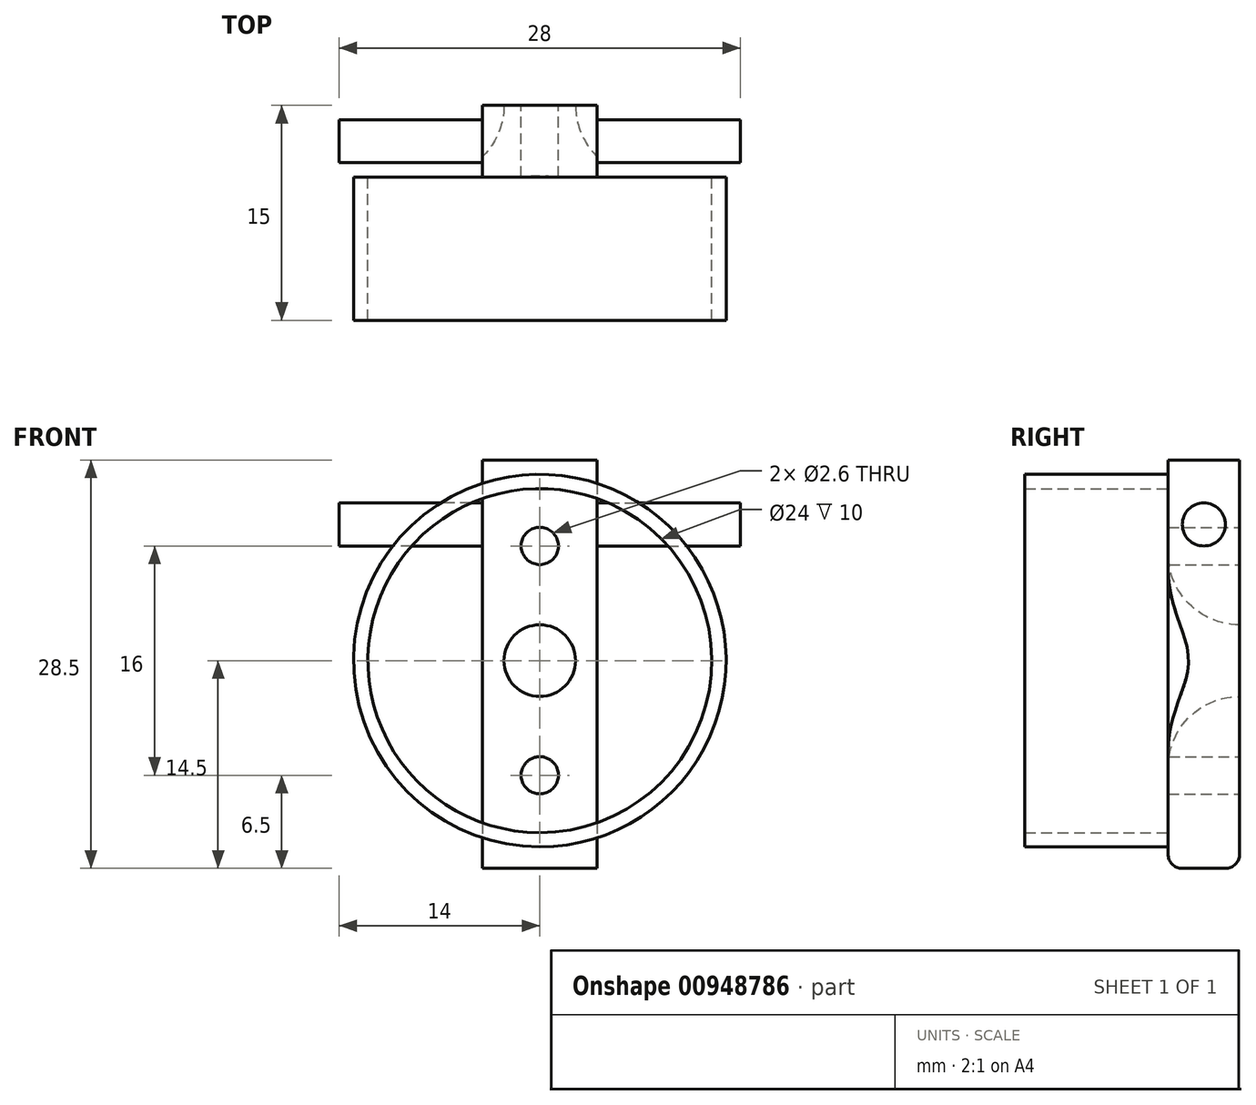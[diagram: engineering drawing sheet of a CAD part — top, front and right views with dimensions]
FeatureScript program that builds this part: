
annotation { "Feature Type Name" : "Feature", "Feature Type Description" : "" }
export const myFeature = defineFeature(function(context is Context, id is Id, definition is map)
    precondition{}
    {
        {
            var Q0;
            Q0=qCreatedBy(makeId("Front.planeOp"),FACE);
            var sketch = newSketch(context, id + "F0", { "sketchPlane" : qUnion([Q0])});
            skLineSegment(sketch, "E0.bottom", {"start": v(14, 14.5) * mm, "end": v(-14, 14.5) * mm});
            skLineSegment(sketch, "E0.top", {"start": v(14, -14.5) * mm, "end": v(-14, -14.5) * mm});
            skLineSegment(sketch, "E0.left", {"start": v(14, 14.5) * mm, "end": v(14, -14.5) * mm});
            skLineSegment(sketch, "E0.right", {"start": v(-14, 14.5) * mm, "end": v(-14, -14.5) * mm});
            skPoint(sketch, "E0.middle", {"position": v(0, 0) * mm});
            skCircle(sketch, "E1", {"center": v(0, 0) * mm, "radius": 12 * mm});
            skCircle(sketch, "E2", {"center": v(0, 0) * mm, "radius": 13 * mm});
            skLineSegment(sketch, "E3", {"start": v(0, 0) * mm, "end": v(0, 8) * mm});
            skLineSegment(sketch, "E4", {"start": v(0, 0) * mm, "end": v(0, -8) * mm});
            skCircle(sketch, "E5", {"center": v(0, 8) * mm, "radius": 1.3 * mm});
            skCircle(sketch, "E6", {"center": v(0, -8) * mm, "radius": 1.3 * mm});
            skCircle(sketch, "E7", {"center": v(0, 0) * mm, "radius": 2.5 * mm});
            skSolve(sketch);
        }
        {
            var Q0;
            Q0=makeQuery(id+"F0.imprint","IMPRINT",FACE,{"disambiguationData":[TD([[makeQuery(id+"F0.imprint","IMPRINT",EDGE,{"derivedFrom":sQuery(id+"F0.wireOp",EDGE,"E1")}),1.0]])]});
            var Q1;
            Q1=makeQuery(id+"F0.imprint","IMPRINT",FACE,{"disambiguationData":[TD([[makeQuery(id+"F0.imprint","IMPRINT",EDGE,{"derivedFrom":sQuery(id+"F0.wireOp",EDGE,"E0.bottom")}),1.0]])]});
            extrude(context, id + "F1", {"entities" : qUnion([Q0, Q1]), "depth" : 5 * mm, "offsetDistance" : 25 * mm});
        }
        {
            var Q0;
            {var subQ0=sQuery(id+"F0.wireOp",EDGE,"jVAeQmTI-I4b5-sMDT-F5OX-ICpV5nC2f3Dc");var subQ1=sQuery(id+"F0.wireOp",EDGE,"E1");var subQ2=makeQuery(id+"F0.imprint","INTERSECT",VERTEX,{"disambiguationData":[OD(1.0)],"derivedFrom":[subQ1,subQ0]});Q0=makeQuery(id+"F0.imprint","IMPRINT",FACE,{"disambiguationData":[TD([[makeQuery(id+"F0.imprint","IMPRINT",EDGE,{"disambiguationData":[TD([[subQ2,-1.0]])],"derivedFrom":subQ1}),-1.0]])]});}
            var Q1;
            {var subQ0=sQuery(id+"F0.wireOp",EDGE,"c9JZCTCg-LH8D-izqR-xvkh-gdVYYUprtubE");var subQ1=sQuery(id+"F0.wireOp",EDGE,"E1");var subQ2=makeQuery(id+"F0.imprint","INTERSECT",VERTEX,{"disambiguationData":[OD(0.0)],"derivedFrom":[subQ1,subQ0]});Q1=makeQuery(id+"F0.imprint","IMPRINT",FACE,{"disambiguationData":[TD([[makeQuery(id+"F0.imprint","IMPRINT",EDGE,{"disambiguationData":[TD([[subQ2,-1.0]])],"derivedFrom":subQ1}),-1.0]])]});}
            extrude(context, id + "F2", {"entities" : qUnion([Q0, Q1]), "operationType" : NewBodyOperationType.ADD, "depth" : 15 * mm, "offsetDistance" : 25 * mm});
        }
        {
            var Q0;
            Q0=makeQuery(id+"F1.opExtrude","CAP_EDGE",EDGE,{"disambiguationData":[OSD([sQuery(id+"F0.wireOp",EDGE,"E7")])],"isStart":false});
            fillet(context, id + "F3", {"entities" : qUnion([Q0]), "radius" : 5 * mm, "tangentPropagation" : true, "allowEdgeOverflow" : false});
        }
        {
            var Q0;
            Q0=makeQuery(id+"F1.opExtrude","SWEPT_FACE",FACE,{"disambiguationData":[OSD([sQuery(id+"F0.wireOp",EDGE,"E0.right")])]});
            var sketch = newSketch(context, id + "F4", { "sketchPlane" : qUnion([Q0])});
            skLineSegment(sketch, "E8", {"start": v(2.5, 14.5) * mm, "end": v(2.5, -14.5) * mm});
            skCircle(sketch, "E9", {"center": v(2.5, 9.5) * mm, "radius": 1.5 * mm});
            skCircle(sketch, "E10", {"center": v(2.5, -10.5) * mm, "radius": 1.5 * mm});
            skSolve(sketch);
        }
        {
            var Q0;
            Q0=makeQuery(id+"F1.opExtrude","SWEPT_FACE",FACE,{"disambiguationData":[OSD([sQuery(id+"F0.wireOp",EDGE,"E0.left")])]});
            var sketch = newSketch(context, id + "F5", { "sketchPlane" : qUnion([Q0])});
            skLineSegment(sketch, "E11", {"start": v(-2.5, 14.5) * mm, "end": v(-2.5, -14.5) * mm});
            skCircle(sketch, "E12", {"center": v(-2.5, 9.5) * mm, "radius": 1.5 * mm});
            skCircle(sketch, "E13", {"center": v(-2.5, -10.5) * mm, "radius": 1.5 * mm});
            skSolve(sketch);
        }
        {
            var Q0;
            {var subQ0=sQuery(id+"F4.wireOp",EDGE,"E9");var subQ1=sQuery(id+"F4.wireOp",EDGE,"E8");var subQ2=makeQuery(id+"F4.imprint","INTERSECT",VERTEX,{"disambiguationData":[OD(0.0)],"derivedFrom":[subQ1,subQ0]});Q0=makeQuery(id+"F4.imprint","IMPRINT",FACE,{"disambiguationData":[TD([[makeQuery(id+"F4.imprint","IMPRINT",EDGE,{"disambiguationData":[TD([[subQ2,-1.0]])],"derivedFrom":subQ1}),1.0]])]});}
            var Q1;
            {var subQ0=sQuery(id+"F4.wireOp",EDGE,"E9");var subQ1=sQuery(id+"F4.wireOp",EDGE,"E8");var subQ2=makeQuery(id+"F4.imprint","INTERSECT",VERTEX,{"disambiguationData":[OD(0.0)],"derivedFrom":[subQ1,subQ0]});Q1=makeQuery(id+"F4.imprint","IMPRINT",FACE,{"disambiguationData":[TD([[makeQuery(id+"F4.imprint","IMPRINT",EDGE,{"disambiguationData":[TD([[subQ2,-1.0]])],"derivedFrom":subQ1}),-1.0]])]});}
            var Q2;
            {var subQ0=sQuery(id+"F4.wireOp",EDGE,"E10");var subQ1=sQuery(id+"F4.wireOp",EDGE,"E8");var subQ2=makeQuery(id+"F4.imprint","INTERSECT",VERTEX,{"disambiguationData":[OD(0.0)],"derivedFrom":[subQ1,subQ0]});Q2=makeQuery(id+"F4.imprint","IMPRINT",FACE,{"disambiguationData":[TD([[makeQuery(id+"F4.imprint","IMPRINT",EDGE,{"disambiguationData":[TD([[subQ2,-1.0]])],"derivedFrom":subQ1}),1.0]])]});}
            var Q3;
            {var subQ0=sQuery(id+"F4.wireOp",EDGE,"E10");var subQ1=sQuery(id+"F4.wireOp",EDGE,"E8");var subQ2=makeQuery(id+"F4.imprint","INTERSECT",VERTEX,{"disambiguationData":[OD(0.0)],"derivedFrom":[subQ1,subQ0]});Q3=makeQuery(id+"F4.imprint","IMPRINT",FACE,{"disambiguationData":[TD([[makeQuery(id+"F4.imprint","IMPRINT",EDGE,{"disambiguationData":[TD([[subQ2,-1.0]])],"derivedFrom":subQ1}),-1.0]])]});}
            extrude(context, id + "F6", {"entities" : qUnion([Q0, Q1, Q2, Q3]), "operationType" : NewBodyOperationType.REMOVE, "oppositeDirection" : true, "depth" : 10 * mm, "offsetDistance" : 25 * mm});
        }
        {
            var Q0;
            {var subQ0=sQuery(id+"F5.wireOp",EDGE,"E12");var subQ1=sQuery(id+"F5.wireOp",EDGE,"E11");var subQ2=makeQuery(id+"F5.imprint","INTERSECT",VERTEX,{"disambiguationData":[OD(0.0)],"derivedFrom":[subQ1,subQ0]});Q0=makeQuery(id+"F5.imprint","IMPRINT",FACE,{"disambiguationData":[TD([[makeQuery(id+"F5.imprint","IMPRINT",EDGE,{"disambiguationData":[TD([[subQ2,-1.0]])],"derivedFrom":subQ1}),1.0]])]});}
            var Q1;
            {var subQ0=sQuery(id+"F5.wireOp",EDGE,"E12");var subQ1=sQuery(id+"F5.wireOp",EDGE,"E11");var subQ2=makeQuery(id+"F5.imprint","INTERSECT",VERTEX,{"disambiguationData":[OD(0.0)],"derivedFrom":[subQ1,subQ0]});Q1=makeQuery(id+"F5.imprint","IMPRINT",FACE,{"disambiguationData":[TD([[makeQuery(id+"F5.imprint","IMPRINT",EDGE,{"disambiguationData":[TD([[subQ2,-1.0]])],"derivedFrom":subQ1}),-1.0]])]});}
            var Q2;
            {var subQ0=sQuery(id+"F5.wireOp",EDGE,"E13");var subQ1=sQuery(id+"F5.wireOp",EDGE,"E11");var subQ2=makeQuery(id+"F5.imprint","INTERSECT",VERTEX,{"disambiguationData":[OD(0.0)],"derivedFrom":[subQ1,subQ0]});Q2=makeQuery(id+"F5.imprint","IMPRINT",FACE,{"disambiguationData":[TD([[makeQuery(id+"F5.imprint","IMPRINT",EDGE,{"disambiguationData":[TD([[subQ2,-1.0]])],"derivedFrom":subQ1}),1.0]])]});}
            var Q3;
            {var subQ0=sQuery(id+"F5.wireOp",EDGE,"E13");var subQ1=sQuery(id+"F5.wireOp",EDGE,"E11");var subQ2=makeQuery(id+"F5.imprint","INTERSECT",VERTEX,{"disambiguationData":[OD(0.0)],"derivedFrom":[subQ1,subQ0]});Q3=makeQuery(id+"F5.imprint","IMPRINT",FACE,{"disambiguationData":[TD([[makeQuery(id+"F5.imprint","IMPRINT",EDGE,{"disambiguationData":[TD([[subQ2,-1.0]])],"derivedFrom":subQ1}),-1.0]])]});}
            extrude(context, id + "F7", {"entities" : qUnion([Q0, Q1, Q2, Q3]), "operationType" : NewBodyOperationType.REMOVE, "oppositeDirection" : true, "depth" : 10 * mm, "offsetDistance" : 25 * mm});
        }
        {
            var Q0;
            Q0=makeQuery(id+"F1.opExtrude","SWEPT_FACE",FACE,{"disambiguationData":[OSD([sQuery(id+"F0.wireOp",EDGE,"E0.bottom")])]});
            extrude(context, id + "F8", {"entities" : qUnion([Q0]), "operationType" : NewBodyOperationType.REMOVE, "oppositeDirection" : true, "depth" : 0.5 * mm, "offsetDistance" : 25 * mm});
        }
        {
            var Q0;
            Q0=makeQuery(id+"F1.opExtrude","CAP_EDGE",EDGE,{"disambiguationData":[OSD([sQuery(id+"F0.wireOp",EDGE,"E0.right")])],"isStart":true});
            var Q1;
            Q1=makeQuery(id+"F1.opExtrude","CAP_EDGE",EDGE,{"disambiguationData":[OSD([sQuery(id+"F0.wireOp",EDGE,"E0.right")])],"isStart":false});
            var Q2;
            Q2=makeQuery(id+"F1.opExtrude","SWEPT_EDGE",EDGE,{"disambiguationData":[OSD([sQuery(id+"F0.wireOp",EDGE,"E0.bottom"),sQuery(id+"F0.wireOp",EDGE,"E0.right")])]});
            var Q3;
            Q3=makeQuery(id+"F1.opExtrude","CAP_EDGE",EDGE,{"disambiguationData":[OSD([sQuery(id+"F0.wireOp",EDGE,"E0.bottom")])],"isStart":false});
            var Q4;
            Q4=makeQuery(id+"F1.opExtrude","CAP_EDGE",EDGE,{"disambiguationData":[OSD([sQuery(id+"F0.wireOp",EDGE,"E0.bottom")])],"isStart":true});
            var Q5;
            Q5=makeQuery(id+"F1.opExtrude","SWEPT_EDGE",EDGE,{"disambiguationData":[OSD([sQuery(id+"F0.wireOp",EDGE,"E0.top"),sQuery(id+"F0.wireOp",EDGE,"E0.right")])]});
            var Q6;
            Q6=makeQuery(id+"F1.opExtrude","CAP_EDGE",EDGE,{"disambiguationData":[OSD([sQuery(id+"F0.wireOp",EDGE,"E0.top")])],"isStart":false});
            var Q7;
            Q7=makeQuery(id+"F1.opExtrude","CAP_EDGE",EDGE,{"disambiguationData":[OSD([sQuery(id+"F0.wireOp",EDGE,"E0.top")])],"isStart":true});
            var Q8;
            Q8=makeQuery(id+"F1.opExtrude","SWEPT_EDGE",EDGE,{"disambiguationData":[OSD([sQuery(id+"F0.wireOp",EDGE,"E0.top"),sQuery(id+"F0.wireOp",EDGE,"E0.left")])]});
            var Q9;
            Q9=makeQuery(id+"F1.opExtrude","CAP_EDGE",EDGE,{"disambiguationData":[OSD([sQuery(id+"F0.wireOp",EDGE,"E0.left")])],"isStart":false});
            var Q10;
            Q10=makeQuery(id+"F1.opExtrude","CAP_EDGE",EDGE,{"disambiguationData":[OSD([sQuery(id+"F0.wireOp",EDGE,"E0.left")])],"isStart":true});
            var Q11;
            Q11=makeQuery(id+"F1.opExtrude","SWEPT_EDGE",EDGE,{"disambiguationData":[OSD([sQuery(id+"F0.wireOp",EDGE,"E0.bottom"),sQuery(id+"F0.wireOp",EDGE,"E0.left")])]});
            var Q12;
            {var subQ0=sQuery(id+"F0.wireOp",EDGE,"E0.bottom");Q12=makeQuery(id+"F8.boolean.opBoolean","COPY",EDGE,{"derivedFrom":makeQuery(id+"F8.opExtrude","CAP_EDGE",EDGE,{"disambiguationData":[OSD([subQ0]),TDD([makeQuery(id+"F1.opExtrude","CAP_EDGE",EDGE,{"disambiguationData":[OSD([subQ0])],"isStart":true})])],"isStart":false})});}
            var Q13;
            Q13=makeQuery(id+"F8.boolean.opBoolean","COPY",EDGE,{"derivedFrom":makeQuery(id+"F8.opExtrude","CAP_EDGE",EDGE,{"disambiguationData":[OSD([sQuery(id+"F0.wireOp",EDGE,"E0.bottom"),sQuery(id+"F0.wireOp",EDGE,"E0.right")])],"isStart":false})});
            var Q14;
            {var subQ0=sQuery(id+"F0.wireOp",EDGE,"E0.bottom");Q14=makeQuery(id+"F8.boolean.opBoolean","COPY",EDGE,{"derivedFrom":makeQuery(id+"F8.opExtrude","CAP_EDGE",EDGE,{"disambiguationData":[OSD([subQ0]),TDD([makeQuery(id+"F1.opExtrude","CAP_EDGE",EDGE,{"disambiguationData":[OSD([subQ0])],"isStart":false})])],"isStart":false})});}
            var Q15;
            Q15=makeQuery(id+"F8.boolean.opBoolean","COPY",EDGE,{"derivedFrom":makeQuery(id+"F8.opExtrude","CAP_EDGE",EDGE,{"disambiguationData":[OSD([sQuery(id+"F0.wireOp",EDGE,"E0.bottom"),sQuery(id+"F0.wireOp",EDGE,"E0.left")])],"isStart":false})});
            fillet(context, id + "F9", {"entities" : qUnion([Q0, Q1, Q2, Q3, Q4, Q5, Q6, Q7, Q8, Q9, Q10, Q11, Q12, Q13, Q14, Q15]), "radius" : 1 * mm, "tangentPropagation" : true, "allowEdgeOverflow" : false});
        }
    });
